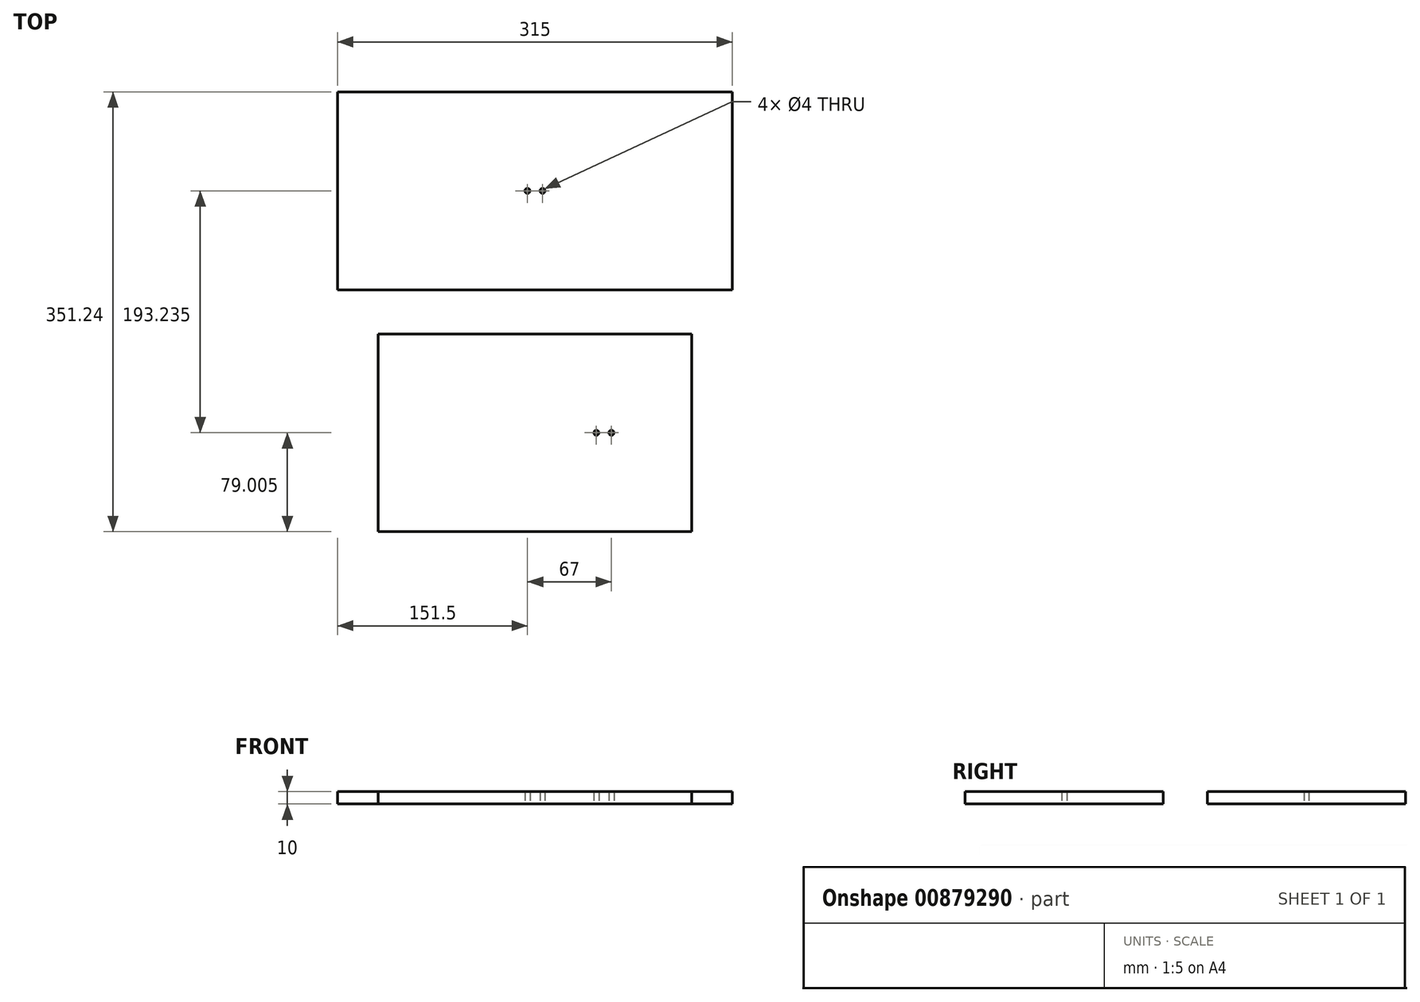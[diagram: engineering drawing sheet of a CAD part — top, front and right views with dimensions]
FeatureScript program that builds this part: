
annotation { "Feature Type Name" : "Feature", "Feature Type Description" : "" }
export const myFeature = defineFeature(function(context is Context, id is Id, definition is map)
    precondition{}
    {
        {
            var Q0;
            Q0=qCreatedBy(makeId("Top.planeOp"),FACE);
            var sketch = newSketch(context, id + "F0", { "sketchPlane" : qUnion([Q0])});
            skLineSegment(sketch, "E0.bottom", {"start": v(-157.5, -79) * mm, "end": v(157.5, -79) * mm});
            skLineSegment(sketch, "E0.top", {"start": v(-157.5, 79) * mm, "end": v(157.5, 79) * mm});
            skLineSegment(sketch, "E0.left", {"start": v(-157.5, -79) * mm, "end": v(-157.5, 79) * mm});
            skLineSegment(sketch, "E0.right", {"start": v(157.5, -79) * mm, "end": v(157.5, 79) * mm});
            skPoint(sketch, "E0.middle", {"position": v(0, 0) * mm});
            skPoint(sketch, "E1.orphan", {"position": v(0, 79) * mm});
            skCircle(sketch, "E2", {"center": v(-6, 0) * mm, "radius": 2 * mm});
            skCircle(sketch, "E3", {"center": v(6, 0) * mm, "radius": 2 * mm});
            skLineSegment(sketch, "E4.bottom", {"start": v(-125, -114.24) * mm, "end": v(125, -114.24) * mm});
            skLineSegment(sketch, "E4.top", {"start": v(-125, -272.24) * mm, "end": v(125, -272.24) * mm});
            skLineSegment(sketch, "E4.left", {"start": v(-125, -114.24) * mm, "end": v(-125, -272.24) * mm});
            skLineSegment(sketch, "E4.right", {"start": v(125, -114.24) * mm, "end": v(125, -272.24) * mm});
            skPoint(sketch, "E4.middle", {"position": v(0, -193.24) * mm});
            skPoint(sketch, "E4.middle.positionSnap0", {"position": v(0, -79) * mm});
            skPoint(sketch, "E4.centerSnap0", {"position": v(0, -79) * mm});
            skCircle(sketch, "E5.MirrorC", {"center": v(49, -193.24) * mm, "radius": 2 * mm});
            skCircle(sketch, "E6.MirrorC", {"center": v(61, -193.24) * mm, "radius": 2 * mm});
            skPoint(sketch, "E7.start.orphan", {"position": v(0, -96.62) * mm});
            skPoint(sketch, "E8.orphan", {"position": v(0, -114.24) * mm});
            skSolve(sketch);
        }
        {
            var Q0;
            Q0=qSketchRegion(id+"F0",true);
            extrude(context, id + "F1", {"entities" : qUnion([Q0]), "depth" : 10 * mm, "offsetDistance" : 25 * mm});
        }
    });
